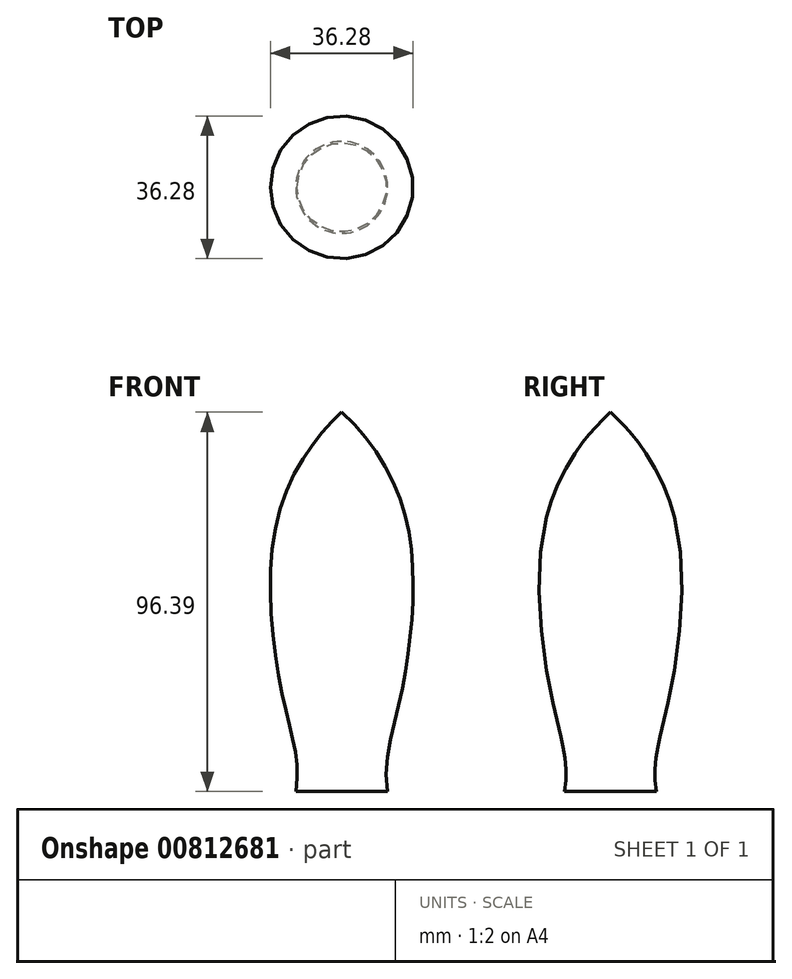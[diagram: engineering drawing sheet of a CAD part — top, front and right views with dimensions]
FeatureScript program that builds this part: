
annotation { "Feature Type Name" : "Feature", "Feature Type Description" : "" }
export const myFeature = defineFeature(function(context is Context, id is Id, definition is map)
    precondition{}
    {
        {
            var Q0;
            Q0=qCreatedBy(makeId("Front.planeOp"),FACE);
            var sketch = newSketch(context, id + "F0", { "sketchPlane" : qUnion([Q0])});
            skFitSpline(sketch, "E0", {"points": [v(0, 96.4) * mm, v(-16.37, 69.12) * mm, v(-14.41, 21.54) * mm, v(-11.68, 0) * mm], "startDerivative": vector(-55.63, -49.2) * mm, "endDerivative": vector(-13.57, -84.44) * mm});
            skLineSegment(sketch, "E1", {"start": v(0, 96.4) * mm, "end": v(0, 0) * mm});
            skLineSegment(sketch, "E2", {"start": v(0, 0) * mm, "end": v(0, 0) * mm});
            skLineSegment(sketch, "E3", {"start": v(-11.68, 0) * mm, "end": v(0, 0) * mm});
            skSolve(sketch);
        }
        {
            var Q0;
            Q0=makeQuery(id+"F0.imprint","IMPRINT",FACE,{"disambiguationData":[TD([[makeQuery(id+"F0.imprint","IMPRINT",EDGE,{"derivedFrom":sQuery(id+"F0.wireOp",EDGE,"E0")}),1.0]])]});
            var Q1;
            Q1=sQuery(id+"F0.wireOp",EDGE,"E1");
            revolve(context, id + "F1", {"surfaceOperationType" : NewSurfaceOperationType.NEW, "entities" : qUnion([Q0]), "axis" : qUnion([Q1]), "revolveType" : RevolveType.FULL});
        }
    });
